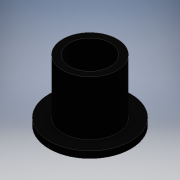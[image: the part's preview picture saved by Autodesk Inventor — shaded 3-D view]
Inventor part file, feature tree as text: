
AUTODESK INVENTOR PART (.ipt)
format: ipt  version: 2016 (Build 200138000, 138)  size: 101,888 bytes
history: native  units: mm
features: extrude x2, other x1, sketch x1
ambient origin geometry x8: Origin, YZ Plane, XZ Plane, XY Plane, X Axis, Y Axis, Z Axis, Center Point
bodies: Body1 (feature_tree)
feature tree (4):
  other  "ソリッド1"
  sketch  "スケッチ1"
  extrude  "押し出し1"  Depth=12.0mm
  extrude  "押し出し2"  Depth=8.0mm
